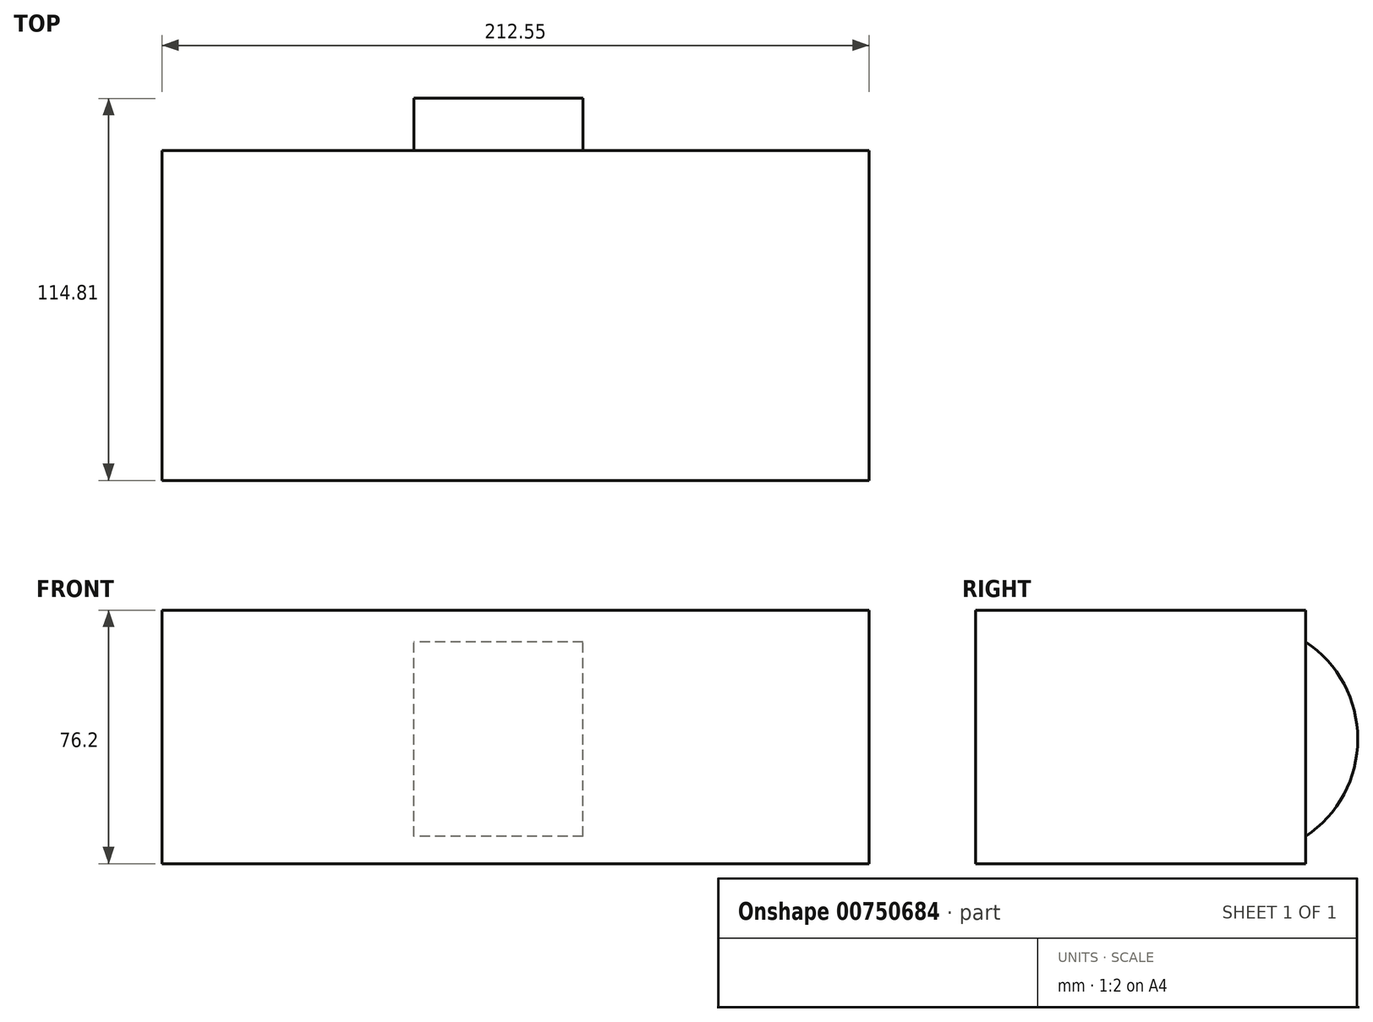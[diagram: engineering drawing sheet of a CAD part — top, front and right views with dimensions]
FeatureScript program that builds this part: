
annotation { "Feature Type Name" : "Feature", "Feature Type Description" : "" }
export const myFeature = defineFeature(function(context is Context, id is Id, definition is map)
    precondition{}
    {
        {
            var Q0;
            Q0=qCreatedBy(makeId("Right.planeOp"),FACE);
            var sketch = newSketch(context, id + "F0", { "sketchPlane" : qUnion([Q0])});
            skCircle(sketch, "E0", {"center": v(0, 37.44) * mm, "radius": 35.12 * mm});
            skSolve(sketch);
        }
        {
            var Q0;
            Q0=makeQuery(id+"F0.imprint","IMPRINT",FACE,{"disambiguationData":[TD([[makeQuery(id+"F0.imprint","IMPRINT",EDGE,{"derivedFrom":sQuery(id+"F0.wireOp",EDGE,"E0")}),1.0]])]});
            extrude(context, id + "F1", {"entities" : qUnion([Q0]), "depth" : 50.8 * mm, "offsetDistance" : 25.4 * mm});
        }
        {
            var Q0;
            Q0=qCreatedBy(makeId("Top.planeOp"),FACE);
            var sketch = newSketch(context, id + "F2", { "sketchPlane" : qUnion([Q0])});
            skLineSegment(sketch, "E1.bottom", {"start": v(-75.72, 19.46) * mm, "end": v(136.83, 19.46) * mm});
            skLineSegment(sketch, "E1.top", {"start": v(-75.72, -79.69) * mm, "end": v(136.83, -79.69) * mm});
            skLineSegment(sketch, "E1.left", {"start": v(-75.72, 19.46) * mm, "end": v(-75.72, -79.69) * mm});
            skLineSegment(sketch, "E1.right", {"start": v(136.83, 19.46) * mm, "end": v(136.83, -79.69) * mm});
            skSolve(sketch);
        }
        {
            var Q0;
            Q0 = qSketchRegion(id + "F2", true);
            extrude(context, id + "F3", {"entities" : qUnion([Q0]), "operationType" : NewBodyOperationType.ADD, "depth" : 76.2 * mm, "offsetDistance" : 25.4 * mm});
        }
    });
